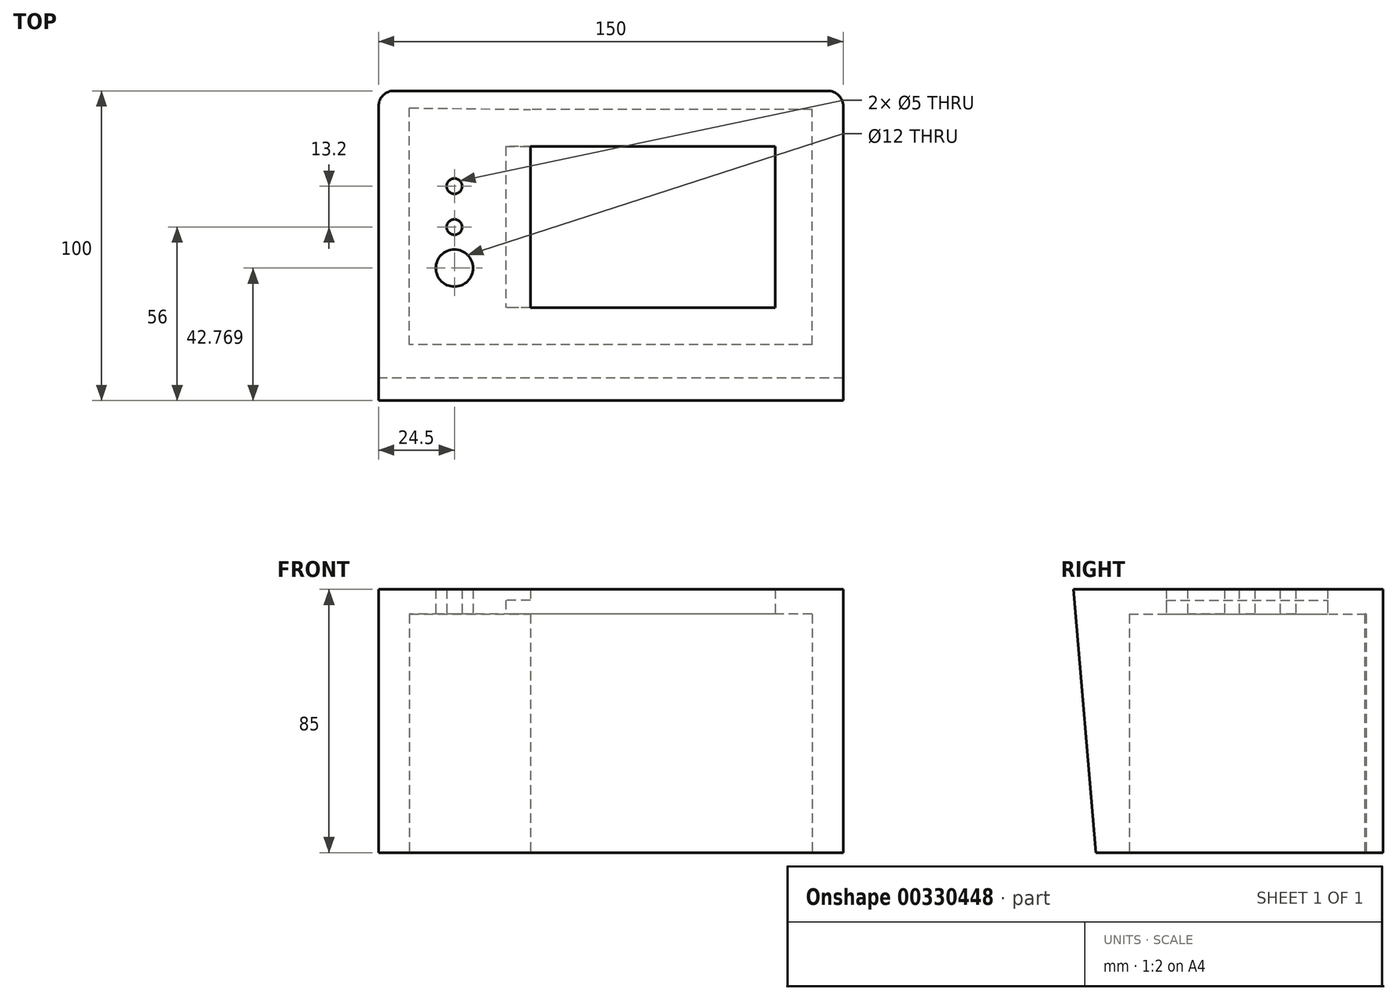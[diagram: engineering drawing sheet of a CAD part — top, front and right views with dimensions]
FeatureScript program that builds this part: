
annotation { "Feature Type Name" : "Feature", "Feature Type Description" : "" }
export const myFeature = defineFeature(function(context is Context, id is Id, definition is map)
    precondition{}
    {
        {
            var Q0;
            Q0=qCreatedBy(makeId("Top.planeOp"),FACE);
            var sketch = newSketch(context, id + "F0", { "sketchPlane" : qUnion([Q0])});
            skLineSegment(sketch, "E0.bottom", {"start": v(0, 0) * mm, "end": v(150, 0) * mm});
            skLineSegment(sketch, "E0.top", {"start": v(5, 100) * mm, "end": v(145, 100) * mm});
            skLineSegment(sketch, "E0.left", {"start": v(0, 0) * mm, "end": v(0, 95) * mm});
            skLineSegment(sketch, "E0.right", {"start": v(150, 0) * mm, "end": v(150, 95) * mm});
            skLineSegment(sketch, "E1.bottom", {"start": v(128, 30) * mm, "end": v(49, 30) * mm});
            skLineSegment(sketch, "E1.top", {"start": v(128, 82) * mm, "end": v(49, 82) * mm});
            skLineSegment(sketch, "E1.left", {"start": v(128, 30) * mm, "end": v(128, 82) * mm});
            skLineSegment(sketch, "E1.right", {"start": v(49, 30) * mm, "end": v(49, 82) * mm});
            skCircle(sketch, "E2", {"center": v(24.5, 42.77) * mm, "radius": 6 * mm});
            skLineSegment(sketch, "E3", {"start": v(49, 56) * mm, "end": v(41.94, 56) * mm, "construction": true});
            skCircle(sketch, "E4", {"center": v(24.5, 56) * mm, "radius": 2.5 * mm});
            skCircle(sketch, "E5", {"center": v(24.5, 69.2) * mm, "radius": 2.5 * mm});
            skLineSegment(sketch, "E6.0", {"start": v(140, 18) * mm, "end": v(49, 18) * mm});
            skLineSegment(sketch, "E6.1", {"start": v(140, 18) * mm, "end": v(140, 94) * mm});
            skLineSegment(sketch, "E6.2", {"start": v(140, 94) * mm, "end": v(49, 94) * mm});
            skLineSegment(sketch, "E7", {"start": v(49, 18) * mm, "end": v(10, 18) * mm});
            skLineSegment(sketch, "E8", {"start": v(10, 18) * mm, "end": v(10, 94.47) * mm});
            skLineSegment(sketch, "E9", {"start": v(10, 94.47) * mm, "end": v(49, 94) * mm});
            skPoint(sketch, "E10.visualSharp", {"position": v(0, 100) * mm});
            skArc(sketch, "E10.filletArc", {"start": v(5, 100) * mm, "mid": v(1.46, 98.54) * mm, "end": v(0, 95) * mm});
            skPoint(sketch, "E11.visualSharp", {"position": v(150, 100) * mm});
            skArc(sketch, "E11.filletArc", {"start": v(150, 95) * mm, "mid": v(148.54, 98.54) * mm, "end": v(145, 100) * mm});
            skSolve(sketch);
        }
        {
            var Q0;
            Q0=makeQuery(id+"F0.imprint","IMPRINT",FACE,{"disambiguationData":[TD([[makeQuery(id+"F0.imprint","IMPRINT",EDGE,{"derivedFrom":sQuery(id+"F0.wireOp",EDGE,"E0.bottom")}),1.0]])]});
            var Q1;
            Q1=makeQuery(id+"F0.imprint","IMPRINT",FACE,{"disambiguationData":[TD([[makeQuery(id+"F0.imprint","IMPRINT",EDGE,{"derivedFrom":sQuery(id+"F0.wireOp",EDGE,"E1.bottom")}),1.0]])]});
            extrude(context, id + "F1", {"entities" : qUnion([Q0, Q1]), "depth" : 85 * mm, "offsetDistance" : 25 * mm});
        }
        {
            var Q0;
            Q0=makeQuery(id+"F0.imprint","IMPRINT",FACE,{"disambiguationData":[TD([[makeQuery(id+"F0.imprint","IMPRINT",EDGE,{"derivedFrom":sQuery(id+"F0.wireOp",EDGE,"E1.bottom")}),1.0]])]});
            extrude(context, id + "F2", {"entities" : qUnion([Q0]), "operationType" : NewBodyOperationType.REMOVE, "depth" : 77 * mm, "offsetDistance" : 25 * mm});
        }
        {
            var Q0;
            Q0=makeQuery(id+"F0.imprint","IMPRINT",FACE,{"disambiguationData":[TD([[makeQuery(id+"F0.imprint","IMPRINT",EDGE,{"derivedFrom":sQuery(id+"F0.wireOp",EDGE,"E1.bottom")}),1.0]])]});
            var sketch = newSketch(context, id + "F3", { "sketchPlane" : qUnion([Q0])});
            skPoint(sketch, "E12.0", {"position": v(49, 82) * mm});
            skPoint(sketch, "E13.0", {"position": v(49, 30) * mm});
            skLineSegment(sketch, "E14", {"start": v(49, 30) * mm, "end": v(41, 30) * mm});
            skLineSegment(sketch, "E15", {"start": v(41, 30) * mm, "end": v(41, 82) * mm});
            skLineSegment(sketch, "E16", {"start": v(41, 82) * mm, "end": v(49, 82) * mm});
            skSolve(sketch);
        }
        {
            var Q0;
            Q0=makeQuery(id+"F3.imprint","IMPRINT",FACE,{"disambiguationData":[TD([[makeQuery(id+"F3.imprint","IMPRINT",EDGE,{"derivedFrom":sQuery(id+"F3.wireOp",EDGE,"E14")}),-1.0]])]});
            extrude(context, id + "F4", {"entities" : qUnion([Q0]), "operationType" : NewBodyOperationType.REMOVE, "depth" : 81.5 * mm, "offsetDistance" : 25 * mm});
        }
        {
            var Q0;
            Q0=makeQuery(id+"F1.opExtrude","SWEPT_FACE",FACE,{"disambiguationData":[OSD([sQuery(id+"F0.wireOp",EDGE,"E0.left")])]});
            var sketch = newSketch(context, id + "F5", { "sketchPlane" : qUnion([Q0])});
            skLineSegment(sketch, "E17", {"start": v(0, 85) * mm, "end": v(-7.2, 0) * mm});
            skSolve(sketch);
        }
        {
            var Q0;
            {var subQ0=sQuery(id+"F5.wireOp",EDGE,"E17");Q0=makeQuery(id+"F5.imprint","IMPRINT",FACE,{"disambiguationData":[TD([[makeQuery(id+"F5.imprint","IMPRINT",EDGE,{"derivedFrom":subQ0}),1.0]])]});}
            extrude(context, id + "F6", {"entities" : qUnion([Q0]), "operationType" : NewBodyOperationType.REMOVE, "endBound" : BoundingType.UP_TO_NEXT, "oppositeDirection" : true, "depth" : 25 * mm, "offsetDistance" : 25 * mm});
        }
    });
